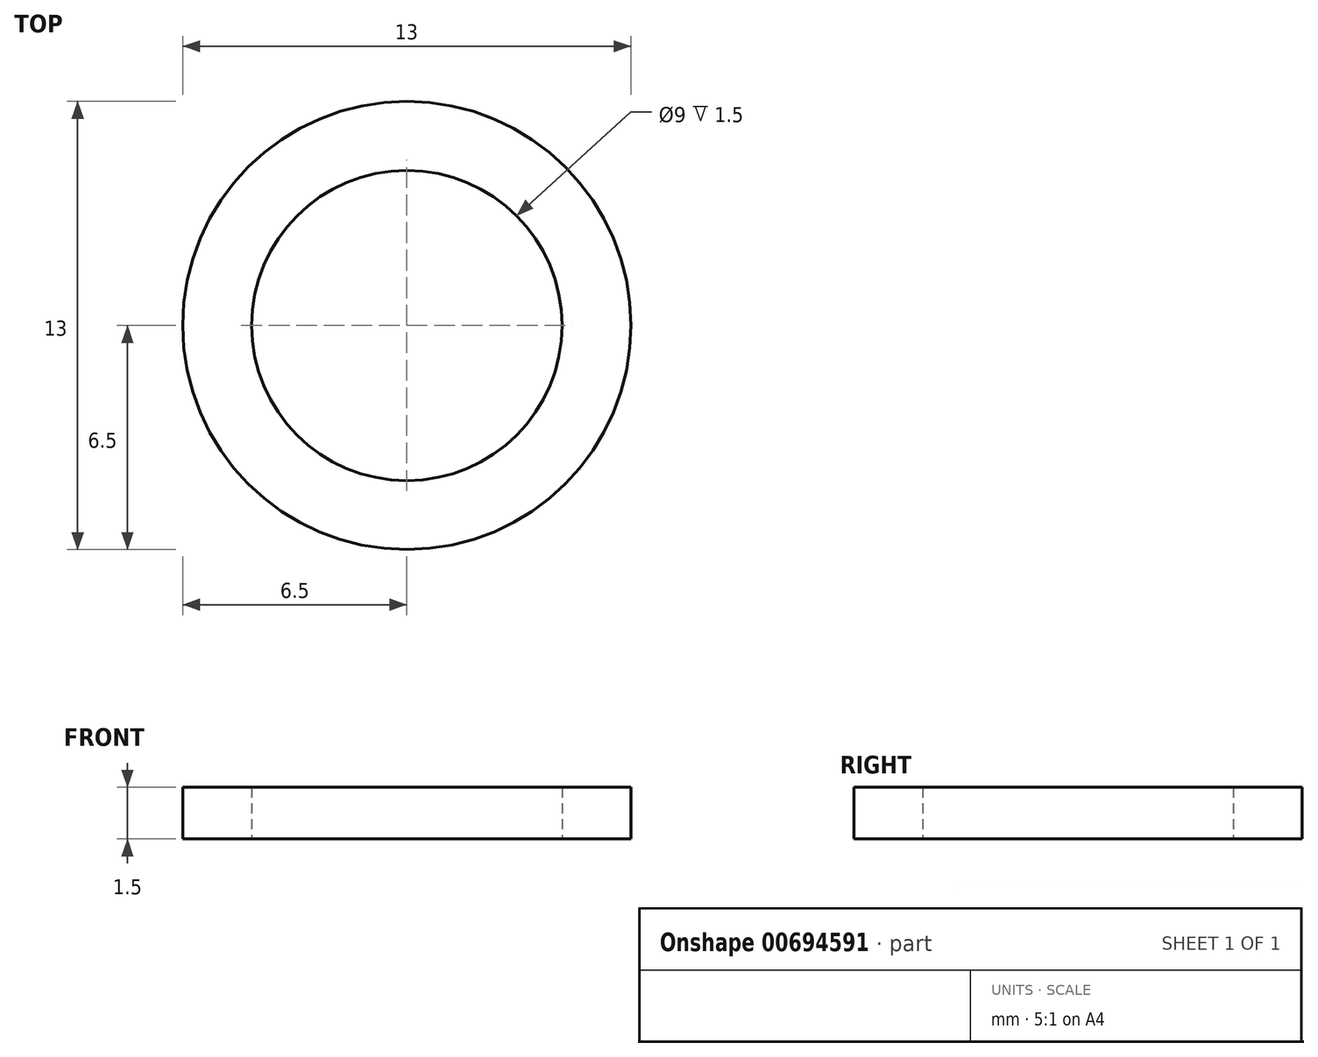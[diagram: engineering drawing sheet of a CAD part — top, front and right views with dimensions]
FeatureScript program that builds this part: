
annotation { "Feature Type Name" : "Feature", "Feature Type Description" : "" }
export const myFeature = defineFeature(function(context is Context, id is Id, definition is map)
    precondition{}
    {
        {
            var Q0;
            Q0=qCreatedBy(makeId("Top.planeOp"),FACE);
            var sketch = newSketch(context, id + "F0", { "sketchPlane" : qUnion([Q0])});
            skCircle(sketch, "E0", {"center": v(0, 0) * mm, "radius": 4.5 * mm});
            skCircle(sketch, "E1", {"center": v(0, 0) * mm, "radius": 6.5 * mm});
            skSolve(sketch);
        }
        {
            var Q0;
            Q0=makeQuery(id+"F0.imprint","IMPRINT",FACE,{"disambiguationData":[TD([[makeQuery(id+"F0.imprint","IMPRINT",EDGE,{"derivedFrom":sQuery(id+"F0.wireOp",EDGE,"E0")}),-1.0]])]});
            extrude(context, id + "F1", {"entities" : qUnion([Q0]), "depth" : 1.5 * mm, "offsetDistance" : 25 * mm});
        }
    });
